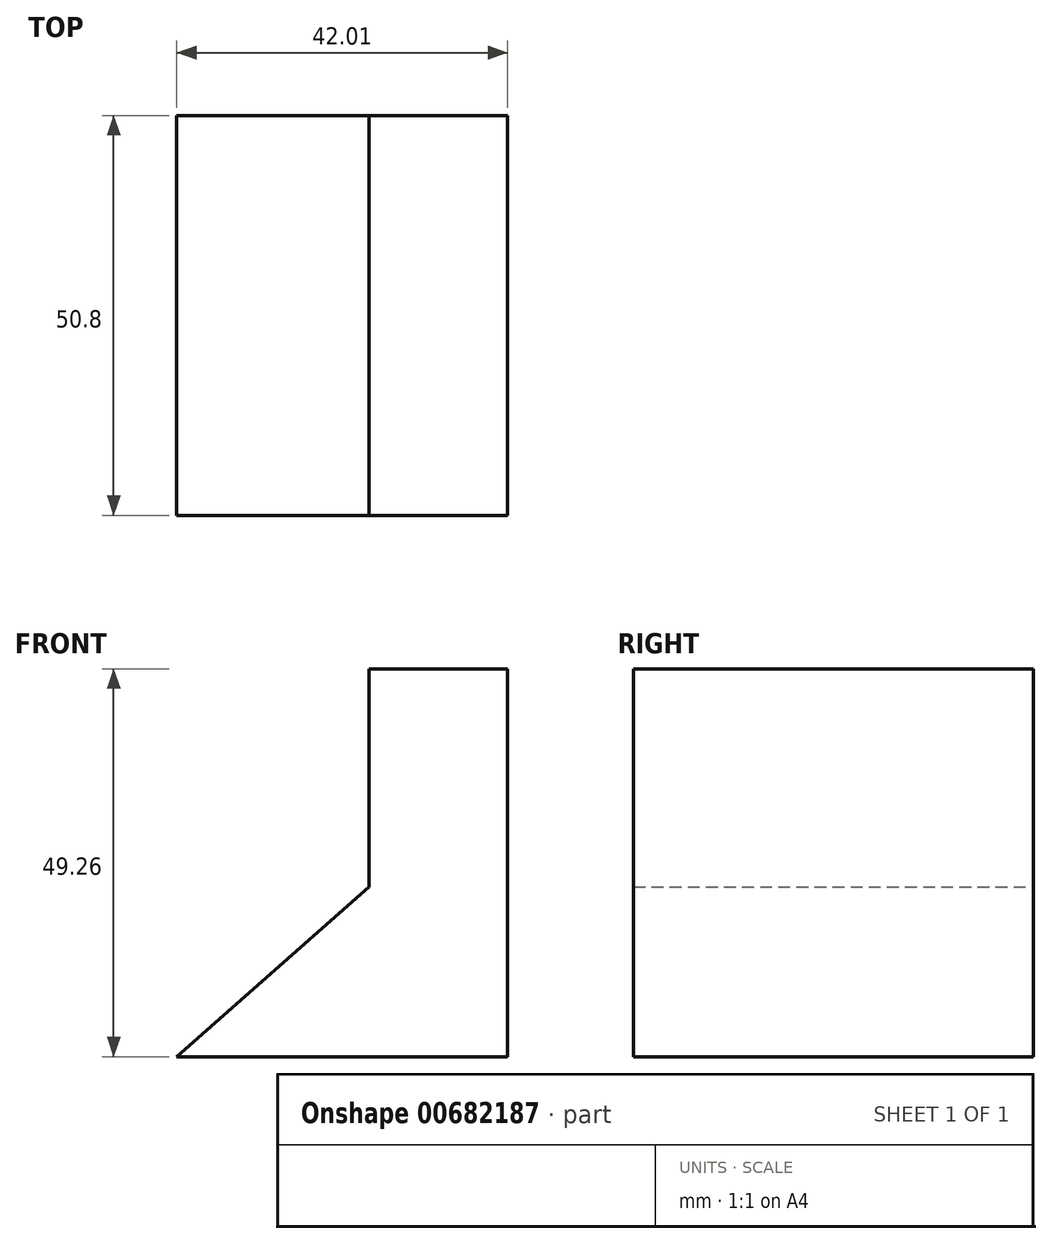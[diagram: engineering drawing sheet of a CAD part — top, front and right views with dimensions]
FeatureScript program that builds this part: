
annotation { "Feature Type Name" : "Feature", "Feature Type Description" : "" }
export const myFeature = defineFeature(function(context is Context, id is Id, definition is map)
    precondition{}
    {
        {
            var Q0;
            Q0=qCreatedBy(makeId("Front.planeOp"),FACE);
            var sketch = newSketch(context, id + "F0", { "sketchPlane" : qUnion([Q0])});
            skLineSegment(sketch, "E0", {"start": v(-6.97, 51.46) * mm, "end": v(-6.97, 2.2) * mm});
            skLineSegment(sketch, "E1", {"start": v(-6.97, 2.2) * mm, "end": v(-48.98, 2.2) * mm});
            skLineSegment(sketch, "E2", {"start": v(-6.97, 51.46) * mm, "end": v(-24.54, 51.46) * mm});
            skLineSegment(sketch, "E3", {"start": v(-24.54, 51.46) * mm, "end": v(-24.54, 23.77) * mm});
            skLineSegment(sketch, "E4", {"start": v(-24.54, 23.77) * mm, "end": v(-48.98, 2.2) * mm});
            skSolve(sketch);
        }
        {
            var Q0;
            Q0 = qSketchRegion(id + "F0", true);
            extrude(context, id + "F1", {"entities" : qUnion([Q0]), "depth" : 50.8 * mm, "offsetDistance" : 25.4 * mm});
        }
    });
